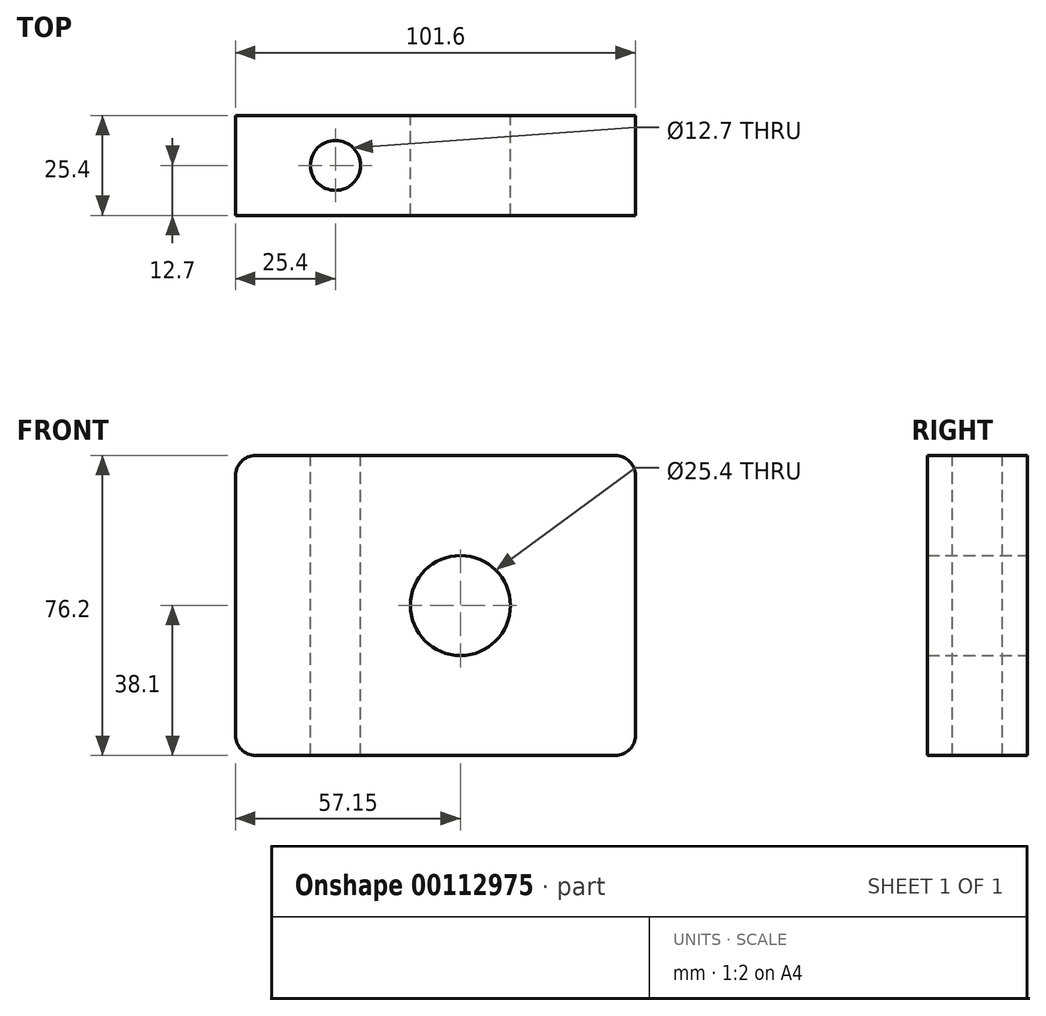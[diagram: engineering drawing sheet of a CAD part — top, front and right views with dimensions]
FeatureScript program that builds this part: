
annotation { "Feature Type Name" : "Feature", "Feature Type Description" : "" }
export const myFeature = defineFeature(function(context is Context, id is Id, definition is map)
    precondition{}
    {
        {
            var Q0;
            Q0=qCreatedBy(makeId("Front.planeOp"),FACE);
            var sketch = newSketch(context, id + "F0", { "sketchPlane" : qUnion([Q0])});
            skLineSegment(sketch, "E0.bottom", {"start": v(50.8, -38.1) * mm, "end": v(-50.8, -38.1) * mm});
            skLineSegment(sketch, "E0.top", {"start": v(50.8, 38.1) * mm, "end": v(-50.8, 38.1) * mm});
            skLineSegment(sketch, "E0.left", {"start": v(50.8, -38.1) * mm, "end": v(50.8, 38.1) * mm});
            skLineSegment(sketch, "E0.right", {"start": v(-50.8, -38.1) * mm, "end": v(-50.8, 38.1) * mm});
            skPoint(sketch, "E0.middle", {"position": v(0, 0) * mm});
            skCircle(sketch, "E1", {"center": v(6.35, 0) * mm, "radius": 12.7 * mm});
            skSolve(sketch);
        }
        {
            var Q0;
            Q0=makeQuery(id+"F0.imprint","IMPRINT",FACE,{"disambiguationData":[TD([[makeQuery(id+"F0.imprint","IMPRINT",EDGE,{"derivedFrom":sQuery(id+"F0.wireOp",EDGE,"E0.bottom")}),-1.0]])]});
            extrude(context, id + "F1", {"entities" : qUnion([Q0]), "depth" : 25.4 * mm, "symmetric" : true});
        }
        {
            var Q0;
            Q0=makeQuery(id+"F1.opExtrude","SWEPT_FACE",FACE,{"disambiguationData":[OSD([sQuery(id+"F0.wireOp",EDGE,"E0.top")])]});
            var sketch = newSketch(context, id + "F2", { "sketchPlane" : qUnion([Q0])});
            skCircle(sketch, "E2", {"center": v(-25.4, 0) * mm, "radius": 6.35 * mm});
            skSolve(sketch);
        }
        {
            var Q0;
            Q0=makeQuery(id+"F2.imprint","IMPRINT",FACE,{"disambiguationData":[TD([[makeQuery(id+"F2.imprint","IMPRINT",EDGE,{"derivedFrom":sQuery(id+"F2.wireOp",EDGE,"E2")}),1.0]])]});
            extrude(context, id + "F3", {"entities" : qUnion([Q0]), "operationType" : NewBodyOperationType.REMOVE, "endBound" : BoundingType.THROUGH_ALL, "oppositeDirection" : true, "depth" : 25.4 * mm});
        }
        {
            var Q0;
            Q0=makeQuery(id+"F1.opExtrude","SWEPT_EDGE",EDGE,{"disambiguationData":[OSD([sQuery(id+"F0.wireOp",EDGE,"E0.top"),sQuery(id+"F0.wireOp",EDGE,"E0.left")])]});
            var Q1;
            Q1=makeQuery(id+"F1.opExtrude","SWEPT_EDGE",EDGE,{"disambiguationData":[OSD([sQuery(id+"F0.wireOp",EDGE,"E0.top"),sQuery(id+"F0.wireOp",EDGE,"E0.right")])]});
            var Q2;
            Q2=makeQuery(id+"F1.opExtrude","SWEPT_EDGE",EDGE,{"disambiguationData":[OSD([sQuery(id+"F0.wireOp",EDGE,"E0.bottom"),sQuery(id+"F0.wireOp",EDGE,"E0.left")])]});
            var Q3;
            Q3=makeQuery(id+"F1.opExtrude","SWEPT_EDGE",EDGE,{"disambiguationData":[OSD([sQuery(id+"F0.wireOp",EDGE,"E0.bottom"),sQuery(id+"F0.wireOp",EDGE,"E0.right")])]});
            fillet(context, id + "F4", {"entities" : qUnion([Q0, Q1, Q2, Q3]), "radius" : 5.08 * mm, "tangentPropagation" : true, "allowEdgeOverflow" : false});
        }
    });
